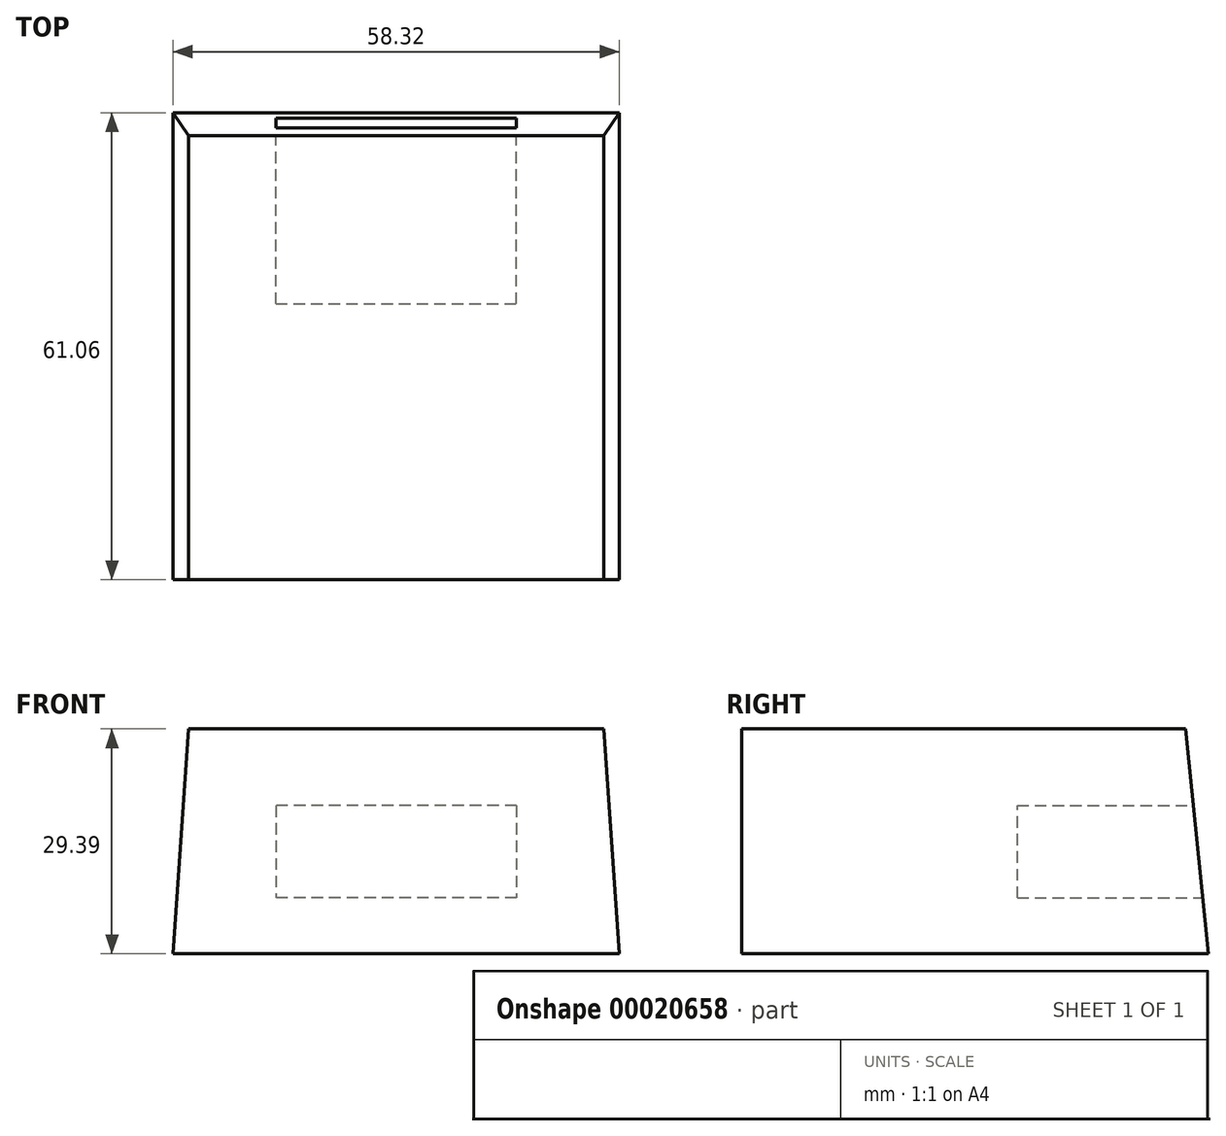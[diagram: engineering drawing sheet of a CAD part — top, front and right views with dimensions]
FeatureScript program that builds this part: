
annotation { "Feature Type Name" : "Feature", "Feature Type Description" : "" }
export const myFeature = defineFeature(function(context is Context, id is Id, definition is map)
    precondition{}
    {
        {
            var Q0;
            Q0=qCreatedBy(makeId("Top.planeOp"),FACE);
            var sketch = newSketch(context, id + "F0", { "sketchPlane" : qUnion([Q0])});
            skLineSegment(sketch, "E0.bottom", {"start": v(-27.19, 25.28) * mm, "end": v(31.13, 25.28) * mm});
            skLineSegment(sketch, "E0.top", {"start": v(-27.19, -35.78) * mm, "end": v(31.13, -35.78) * mm});
            skLineSegment(sketch, "E0.left", {"start": v(-27.19, 25.28) * mm, "end": v(-27.19, -35.78) * mm});
            skLineSegment(sketch, "E0.right", {"start": v(31.13, 25.28) * mm, "end": v(31.13, -35.78) * mm});
            skPoint(sketch, "E1", {"position": v(1.97, 25.28) * mm});
            skSolve(sketch);
        }
        {
            var Q0;
            Q0=qCreatedBy(makeId("Top.planeOp"),FACE);
            cPlane(context, id + "F1", {"entities" : qUnion([Q0]), "cplaneType" : CPlaneType.OFFSET, "offset" : 29.4 * mm, "width" : 150 * mm, "height" : 150 * mm});
        }
        {
            var Q0;
            Q0=qCreatedBy(id+"F1.planeOp",FACE);
            var sketch = newSketch(context, id + "F2", { "sketchPlane" : qUnion([Q0])});
            skLineSegment(sketch, "E2.bottom", {"start": v(-25.19, 22.28) * mm, "end": v(29.13, 22.28) * mm});
            skLineSegment(sketch, "E2.top", {"start": v(-25.19, -35.78) * mm, "end": v(29.13, -35.78) * mm});
            skLineSegment(sketch, "E2.left", {"start": v(-25.19, 22.28) * mm, "end": v(-25.19, -35.78) * mm});
            skLineSegment(sketch, "E2.right", {"start": v(29.13, 22.28) * mm, "end": v(29.13, -35.78) * mm});
            skSolve(sketch);
        }
        {
            var Q0;
            Q0=makeQuery(id+"F0.imprint","IMPRINT",FACE,{"disambiguationData":[TD([[makeQuery(id+"F0.imprint","IMPRINT",EDGE,{"derivedFrom":sQuery(id+"F0.wireOp",EDGE,"E0.bottom")}),-1.0]])]});
            var Q1;
            Q1=makeQuery(id+"F2.imprint","IMPRINT",FACE,{"disambiguationData":[TD([[makeQuery(id+"F2.imprint","IMPRINT",EDGE,{"derivedFrom":sQuery(id+"F2.wireOp",EDGE,"E2.bottom")}),-1.0]])]});
            loft(context, id + "F3", {"sheetProfilesArray" : [{ "sheetProfileEntities" : qUnion([Q0]) }, { "sheetProfileEntities" : qUnion([Q1]) }]});
        }
        {
            var Q0;
            Q0=makeQuery(id+"F3.opLoft","MID_CAP_EDGE",EDGE,{"disambiguationData":[OSD([sQuery(id+"F0.wireOp",EDGE,"E0.bottom"),sQuery(id+"F0.wireOp",EDGE,"E0.left"),sQuery(id+"F0.wireOp",EDGE,"E0.right")])],"capPos":0.0});
            var Q1;
            Q1=qCreatedBy(makeId("Front.planeOp"),FACE);
            cPlane(context, id + "F4", {"entities" : qUnion([Q0, Q1]), "cplaneType" : CPlaneType.LINE_ANGLE, "offset" : 25 * mm, "angle" : 0 * degree, "width" : 150 * mm, "height" : 150 * mm});
        }
        {
            var Q0;
            Q0=qCreatedBy(id+"F4.planeOp",FACE);
            var sketch = newSketch(context, id + "F5", { "sketchPlane" : qUnion([Q0])});
            skLineSegment(sketch, "E3.bottom", {"start": v(13.76, 7.3) * mm, "end": v(-17.7, 7.29) * mm});
            skLineSegment(sketch, "E3.top", {"start": v(13.76, 19.4) * mm, "end": v(-17.7, 19.39) * mm});
            skLineSegment(sketch, "E3.left", {"start": v(13.76, 7.3) * mm, "end": v(13.76, 19.39) * mm});
            skLineSegment(sketch, "E3.right", {"start": v(-17.7, 7.3) * mm, "end": v(-17.7, 19.39) * mm});
            skPoint(sketch, "E4", {"position": v(-1.97, 7.3) * mm});
            skSolve(sketch);
        }
        {
            var Q0;
            Q0=makeQuery(id+"F5.imprint","IMPRINT",FACE,{"disambiguationData":[TD([[makeQuery(id+"F5.imprint","IMPRINT",EDGE,{"derivedFrom":sQuery(id+"F5.wireOp",EDGE,"E3.bottom")}),-1.0]])]});
            extrude(context, id + "F6", {"entities" : qUnion([Q0]), "operationType" : NewBodyOperationType.REMOVE, "oppositeDirection" : true, "depth" : 25 * mm});
        }
    });
